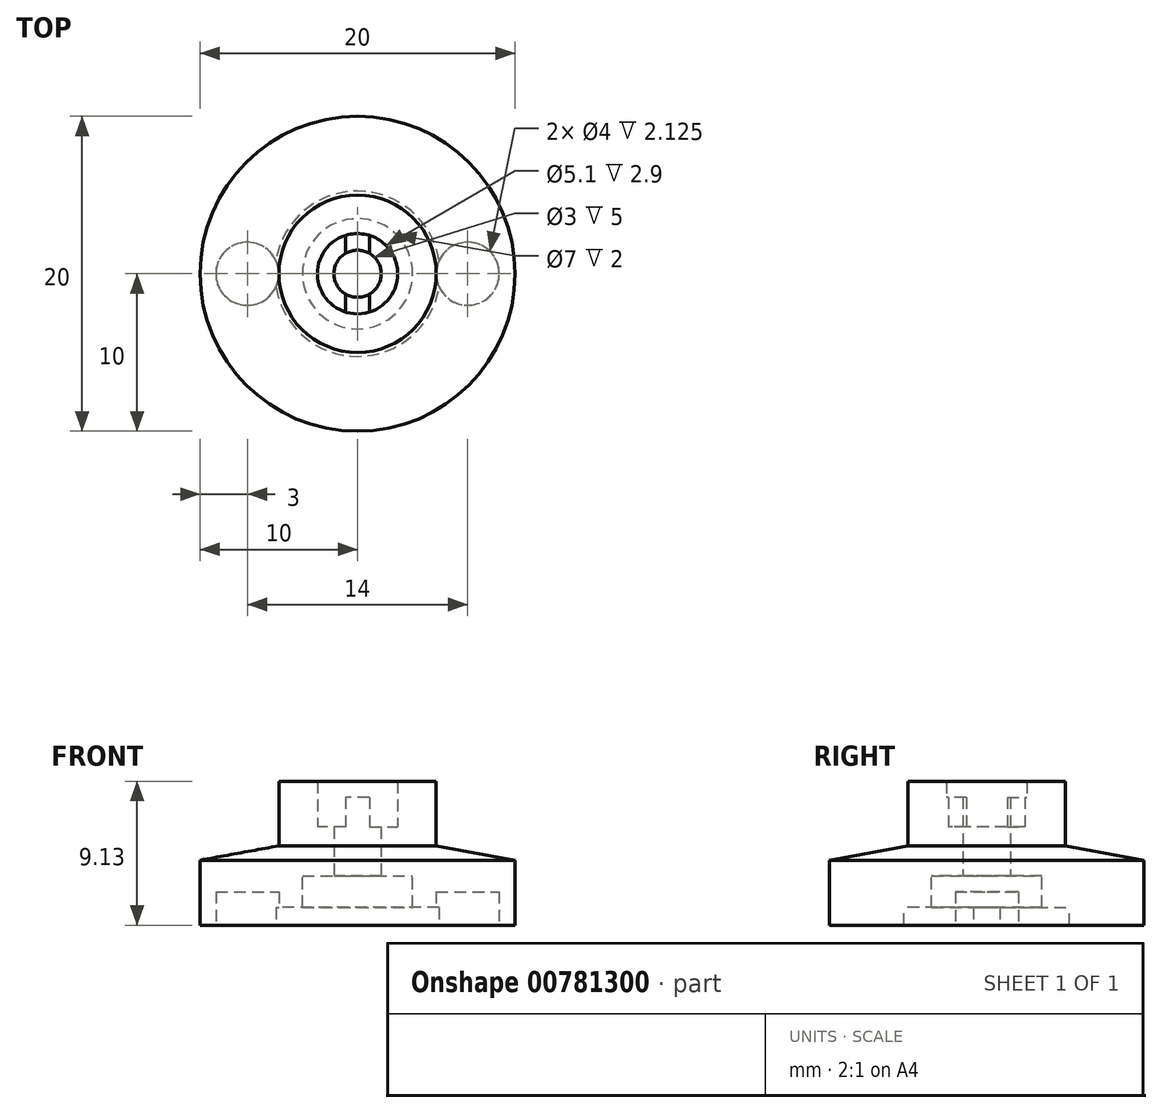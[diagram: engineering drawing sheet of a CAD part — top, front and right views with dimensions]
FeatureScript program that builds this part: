
annotation { "Feature Type Name" : "Feature", "Feature Type Description" : "" }
export const myFeature = defineFeature(function(context is Context, id is Id, definition is map)
    precondition{}
    {
        {
            var Q0;
            Q0=qCreatedBy(makeId("Top.planeOp"),FACE);
            var sketch = newSketch(context, id + "F0", { "sketchPlane" : qUnion([Q0])});
            skCircle(sketch, "E0", {"center": v(0, 0) * mm, "radius": 2.55 * mm});
            skCircle(sketch, "E1", {"center": v(0, 0) * mm, "radius": 5 * mm});
            skCircle(sketch, "E2", {"center": v(0, 0) * mm, "radius": 1.5 * mm});
            skLineSegment(sketch, "E3", {"start": v(-0.75, 1.3) * mm, "end": v(-0.75, 2.44) * mm});
            skLineSegment(sketch, "E4", {"start": v(0.75, 1.3) * mm, "end": v(0.75, 2.44) * mm});
            skLineSegment(sketch, "E5", {"start": v(-0.75, -1.3) * mm, "end": v(-0.75, -2.44) * mm});
            skLineSegment(sketch, "E6", {"start": v(0.75, -1.3) * mm, "end": v(0.75, -2.44) * mm});
            skSolve(sketch);
        }
        {
            var Q0;
            Q0=makeQuery(id+"F0.imprint","IMPRINT",FACE,{"disambiguationData":[TD([[makeQuery(id+"F0.imprint","IMPRINT",EDGE,{"derivedFrom":sQuery(id+"F0.wireOp",EDGE,"E1")}),1.0]])]});
            extrude(context, id + "F1", {"entities" : qUnion([Q0]), "depth" : 6 * mm, "offsetDistance" : 25 * mm});
        }
        {
            var Q0;
            {var subQ0=sQuery(id+"F0.wireOp",EDGE,"E3");Q0=makeQuery(id+"F0.imprint","IMPRINT",FACE,{"disambiguationData":[TD([[makeQuery(id+"F0.imprint","IMPRINT",EDGE,{"derivedFrom":subQ0}),-1.0]])]});}
            var Q1;
            {var subQ0=sQuery(id+"F0.wireOp",EDGE,"E5");Q1=makeQuery(id+"F0.imprint","IMPRINT",FACE,{"disambiguationData":[TD([[makeQuery(id+"F0.imprint","IMPRINT",EDGE,{"derivedFrom":subQ0}),1.0]])]});}
            extrude(context, id + "F2", {"entities" : qUnion([Q0, Q1]), "operationType" : NewBodyOperationType.ADD, "depth" : 5 * mm, "offsetDistance" : 25 * mm});
        }
        {
            var Q0;
            {var subQ0=sQuery(id+"F0.wireOp",EDGE,"E3");Q0=makeQuery(id+"F0.imprint","IMPRINT",FACE,{"disambiguationData":[TD([[makeQuery(id+"F0.imprint","IMPRINT",EDGE,{"derivedFrom":subQ0}),1.0]])]});}
            var Q1;
            {var subQ0=sQuery(id+"F0.wireOp",EDGE,"E4");Q1=makeQuery(id+"F0.imprint","IMPRINT",FACE,{"disambiguationData":[TD([[makeQuery(id+"F0.imprint","IMPRINT",EDGE,{"derivedFrom":subQ0}),-1.0]])]});}
            extrude(context, id + "F3", {"entities" : qUnion([Q0, Q1]), "operationType" : NewBodyOperationType.ADD, "depth" : 3.1 * mm, "offsetDistance" : 25 * mm});
        }
        {
            var Q0;
            Q0=qCreatedBy(makeId("Front.planeOp"),FACE);
            var sketch = newSketch(context, id + "F4", { "sketchPlane" : qUnion([Q0])});
            skLineSegment(sketch, "E7", {"start": v(0, 0) * mm, "end": v(-10, 0) * mm});
            skLineSegment(sketch, "E8", {"start": v(-10, 0) * mm, "end": v(-10, 1) * mm});
            skLineSegment(sketch, "E9", {"start": v(-10, 1) * mm, "end": v(-4.5, 2) * mm});
            skLineSegment(sketch, "E10", {"start": v(-4.5, 2) * mm, "end": v(-4, 2) * mm});
            skLineSegment(sketch, "E11", {"start": v(-4, 2) * mm, "end": v(-4, 0) * mm});
            skLineSegment(sketch, "E12", {"start": v(0, -1.5) * mm, "end": v(0, 4) * mm, "construction": true});
            skSolve(sketch);
        }
        {
            var Q0;
            Q0=qSketchRegion(id+"F4",true);
            var Q1;
            Q1=sQuery(id+"F4.wireOp",EDGE,"E12");
            revolve(context, id + "F5", {"operationType" : NewBodyOperationType.ADD, "surfaceOperationType" : NewSurfaceOperationType.NEW, "entities" : qUnion([Q0]), "axis" : qUnion([Q1]), "revolveType" : RevolveType.FULL});
        }
        {
            var Q0;
            {var subQ0=sQuery(id+"F0.wireOp",EDGE,"E6");var subQ1=sQuery(id+"F0.wireOp",EDGE,"E4");var subQ2=sQuery(id+"F0.wireOp",EDGE,"E2");var subQ3=sQuery(id+"F0.wireOp",EDGE,"E0");var subQ4=sQuery(id+"F0.wireOp",EDGE,"E5");var subQ5=sQuery(id+"F0.wireOp",EDGE,"E3");Q0=makeQuery(id+"F5.boolean.opBoolean","MERGE",FACE,{"derivedFrom":[makeQuery(id+"F3.boolean.opBoolean","MERGE",FACE,{"derivedFrom":[makeQuery(id+"F2.boolean.opBoolean","MERGE",FACE,{"derivedFrom":[makeQuery(id+"F1.opExtrude","CAP_FACE",FACE,{"disambiguationData":[OSD([subQ3,sQuery(id+"F0.wireOp",EDGE,"E1")])],"isStart":true}),makeQuery(id+"F2.opExtrude","CAP_FACE",FACE,{"disambiguationData":[OSD([subQ3,subQ2,subQ5,subQ1])],"isStart":true}),makeQuery(id+"F2.opExtrude","CAP_FACE",FACE,{"disambiguationData":[OSD([subQ3,subQ2,subQ4,subQ0])],"isStart":true})]}),makeQuery(id+"F3.opExtrude","CAP_FACE",FACE,{"disambiguationData":[OSD([subQ3,subQ2,subQ5,subQ4])],"isStart":true}),makeQuery(id+"F3.opExtrude","CAP_FACE",FACE,{"disambiguationData":[OSD([subQ3,subQ2,subQ1,subQ0])],"isStart":true})]}),makeQuery(id+"F5.opRevolve","SWEPT_FACE",FACE,{"disambiguationData":[OSD([sQuery(id+"F4.wireOp",EDGE,"E7")])]})]});}
            var sketch = newSketch(context, id + "F6", { "sketchPlane" : qUnion([Q0])});
            skCircle(sketch, "E13", {"center": v(0, 0) * mm, "radius": 3.5 * mm});
            skSolve(sketch);
        }
        {
            var Q0;
            Q0=makeQuery(id+"F6.imprint","IMPRINT",FACE,{"disambiguationData":[TD([[makeQuery(id+"F6.imprint","IMPRINT",EDGE,{"derivedFrom":sQuery(id+"F6.wireOp",EDGE,"E13")}),-1.0]])]});
            extrude(context, id + "F7", {"entities" : qUnion([Q0]), "operationType" : NewBodyOperationType.ADD, "depth" : 2 * mm, "offsetDistance" : 25 * mm});
        }
        {
            var Q0;
            Q0=makeQuery(id+"F7.opExtrude","CAP_FACE",FACE,{"disambiguationData":[OSD([sQuery(id+"F4.wireOp",EDGE,"E7"),sQuery(id+"F4.wireOp",EDGE,"E8"),sQuery(id+"F6.wireOp",EDGE,"E13")])],"isStart":false});
            var sketch = newSketch(context, id + "F8", { "sketchPlane" : qUnion([Q0])});
            skCircle(sketch, "E14", {"center": v(0, 0) * mm, "radius": 5.25 * mm});
            skSolve(sketch);
        }
        {
            var Q0;
            Q0=makeQuery(id+"F8.imprint","IMPRINT",FACE,{"disambiguationData":[TD([[makeQuery(id+"F8.imprint","IMPRINT",EDGE,{"derivedFrom":sQuery(id+"F8.wireOp",EDGE,"E14")}),-1.0]])]});
            extrude(context, id + "F9", {"entities" : qUnion([Q0]), "operationType" : NewBodyOperationType.ADD, "depth" : 1.12 * mm, "offsetDistance" : 25 * mm});
        }
        {
            var Q0;
            Q0=makeQuery(id+"F9.opExtrude","CAP_FACE",FACE,{"disambiguationData":[OSD([sQuery(id+"F4.wireOp",EDGE,"E7"),sQuery(id+"F4.wireOp",EDGE,"E8"),sQuery(id+"F8.wireOp",EDGE,"E14")])],"isStart":false});
            var sketch = newSketch(context, id + "F10", { "sketchPlane" : qUnion([Q0])});
            skPoint(sketch, "E15", {"position": v(-7, 0) * mm});
            skPoint(sketch, "E16", {"position": v(7, 0) * mm});
            skLineSegment(sketch, "E17", {"start": v(-7, 2) * mm, "end": v(-4.85, 2) * mm});
            skLineSegment(sketch, "E18", {"start": v(-7, -2) * mm, "end": v(-4.85, -2) * mm});
            skLineSegment(sketch, "E19", {"start": v(7, -2) * mm, "end": v(4.85, -2) * mm});
            skLineSegment(sketch, "E20", {"start": v(7, 2) * mm, "end": v(4.85, 2) * mm});
            skCircle(sketch, "E21", {"center": v(-7, 0) * mm, "radius": 2 * mm});
            skCircle(sketch, "E22", {"center": v(7, 0) * mm, "radius": 2 * mm});
            skSolve(sketch);
        }
        {
            var Q0;
            Q0=qSketchRegion(id+"F10",true);
            extrude(context, id + "F11", {"entities" : qUnion([Q0]), "operationType" : NewBodyOperationType.REMOVE, "oppositeDirection" : true, "depth" : 2.12 * mm, "offsetDistance" : 25 * mm});
        }
    });
